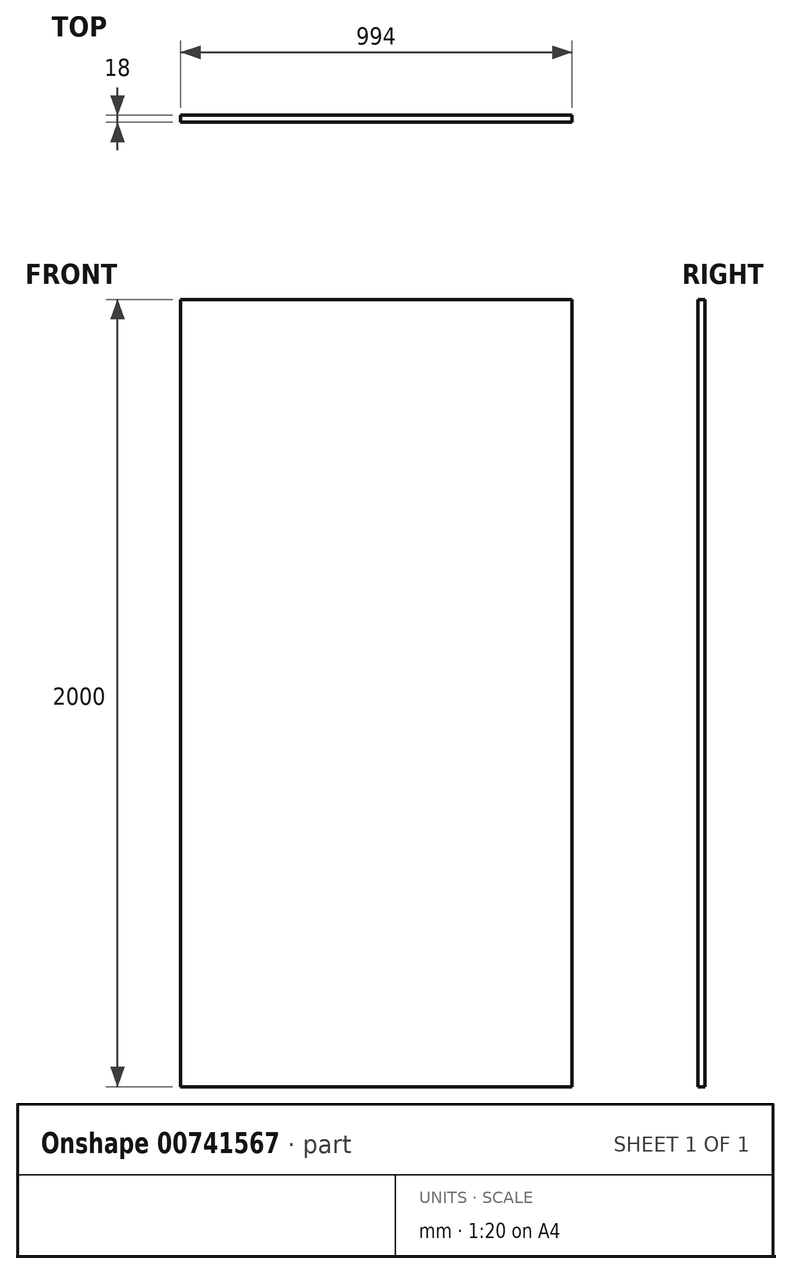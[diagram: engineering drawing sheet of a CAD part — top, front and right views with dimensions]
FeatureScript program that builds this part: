
annotation { "Feature Type Name" : "Feature", "Feature Type Description" : "" }
export const myFeature = defineFeature(function(context is Context, id is Id, definition is map)
    precondition{}
    {
        {
            var Q0;
            Q0=qCreatedBy(makeId("Front.planeOp"),FACE);
            var sketch = newSketch(context, id + "F0", { "sketchPlane" : qUnion([Q0])});
            skLineSegment(sketch, "E0.bottom", {"start": v(-497, -1000) * mm, "end": v(497, -1000) * mm});
            skLineSegment(sketch, "E0.top", {"start": v(-497, 1000) * mm, "end": v(497, 1000) * mm});
            skLineSegment(sketch, "E0.left", {"start": v(-497, -1000) * mm, "end": v(-497, 1000) * mm});
            skLineSegment(sketch, "E0.right", {"start": v(497, -1000) * mm, "end": v(497, 1000) * mm});
            skPoint(sketch, "E0.middle", {"position": v(0, 0) * mm});
            skSolve(sketch);
        }
        {
            var Q0;
            Q0=qSketchRegion(id+"F0",true);
            extrude(context, id + "F1", {"entities" : qUnion([Q0]), "oppositeDirection" : true, "depth" : 18 * mm, "offsetDistance" : 25 * mm});
        }
    });
